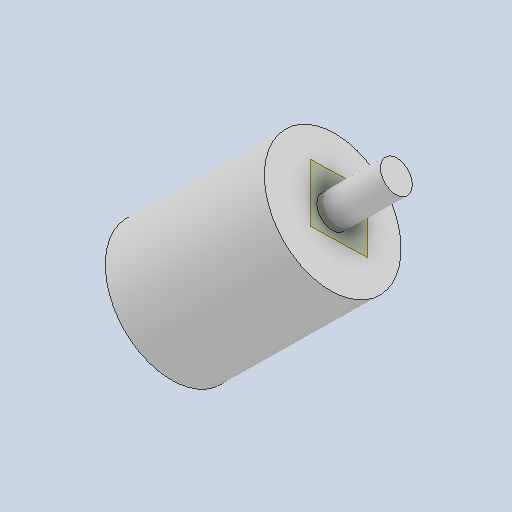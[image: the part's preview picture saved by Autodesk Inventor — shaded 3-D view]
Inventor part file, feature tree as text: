
AUTODESK INVENTOR PART (.ipt)
format: ipt  version: 2022 (Build 260153000, 153)  size: 110,080 bytes
history: native  units: mm
features: other x3, extrude x2, sketch x2, plane x1
ambient origin geometry x8: Origin, YZ Plane, XZ Plane, XY Plane, X Axis, Y Axis, Z Axis, Center Point
bodies: Solid1 (feature_tree)
feature tree (8):
  plane  "Work Plane1"
  extrude  "Extrusion1"  Depth=1.0mm TaperAngle=0.0deg
  extrude  "Extrusion2"  Depth=25.0mm
  sketch  "Sketch1"  dims[d0=4.9mm d1=1.0mm d2=0.0mm]
  sketch  "Sketch2"  dims[d3=9.0mm d4=0.0mm d5=21.0mm d6=25.0mm d7=0.0mm]
  other  "Assembly_Final.iam"
  other  "Caja_Reductora:1"
  other  "Acople_Motor:1"
